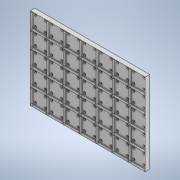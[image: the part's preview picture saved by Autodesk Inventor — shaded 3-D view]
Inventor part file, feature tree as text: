
AUTODESK INVENTOR PART (.ipt)
format: ipt  version: 2021 (Build 250183000, 183)  size: 888,320 bytes
history: native  units: mm
features: extrude x4, sketch x3, chamfer x2, pattern_linear x1
ambient origin geometry x8: Origin, YZ Plane, XZ Plane, XY Plane, X Axis, Y Axis, Z Axis, Center Point
bodies: Solid1 (feature_tree)
feature tree (10):
  extrude  "Frame"  TaperAngle=0.0deg  [1 undecoded]
  extrude  "Frame_center_hole"  Depth=42.0mm
  chamfer  "frame_camfer"  Distance=1.6mm
  extrude  "mounting_holes_outer"  Depth=42.0mm
  extrude  "mounting_holes_inner"  Depth=42.0mm
  chamfer  "mounting_holes_countersink"  Distance=1.6mm
  pattern_linear  "Rectangular Pattern1"  Spacing1=2.846mm  [1 undecoded]
  sketch  "Sketch1"  dims[d1=0.0mm d2=0.0mm d3=0.0mm]
  sketch  "Sketch3"  dims[d7=42.0mm d8=42.0mm]
  sketch  "Sketch4"  dims[d9=2.846mm d10=1.6mm d11=1.6mm d12=1.6mm d13=1.6mm d14=2.846mm d15=2.0mm d16=45.0deg d20=50.0mm d22=42.0mm d23=6.5mm d24=6.5mm d25=6.5mm d26=6.5mm d27=26.0mm d28=26.0mm d29=6.4mm d30=0.0mm d35=3.5mm d36=3.5mm d37=3.5mm d38=3.5mm d39=4.0mm d40=0.0mm d41=2.5mm d42=2.0mm d43=45.0deg d44=70.0mm d46=42.0mm]
note: 2 required parameter values undecoded (feature->parameter linkage not recoverable at this tier; creation-order binding heuristic only, values carry confidence <= 0.55)
